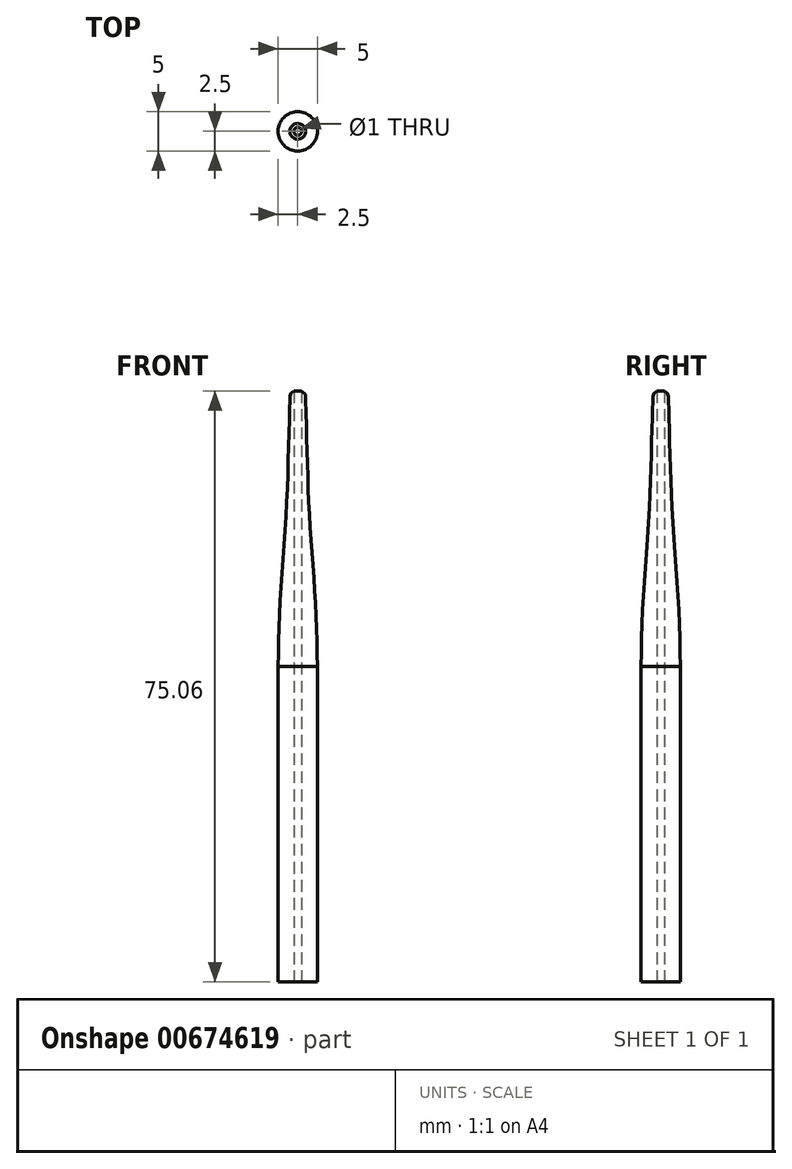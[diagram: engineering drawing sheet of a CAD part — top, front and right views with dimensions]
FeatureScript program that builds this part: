
annotation { "Feature Type Name" : "Feature", "Feature Type Description" : "" }
export const myFeature = defineFeature(function(context is Context, id is Id, definition is map)
    precondition{}
    {
        {
            var Q0;
            Q0=qCreatedBy(makeId("Right.planeOp"),FACE);
            var sketch = newSketch(context, id + "F0", { "sketchPlane" : qUnion([Q0])});
            skLineSegment(sketch, "E0.right", {"start": v(-2.5, 12.56) * mm, "end": v(-2.5, 0) * mm});
            skPoint(sketch, "E0.middle", {"position": v(0, 0) * mm});
            skLineSegment(sketch, "E1.right", {"start": v(-0.5, 0) * mm, "end": v(-0.5, 47.56) * mm});
            skFitSpline(sketch, "E2", {"points": [v(-2.5, 12.56) * mm, v(-2.22, 21.1) * mm, v(-1.53, 30.92) * mm, v(-1.16, 40.59) * mm, v(-1, 46.59) * mm, v(-0.92, 47.22) * mm, v(-0.5, 47.56) * mm], "startDerivative": vector(0.72, 37.68) * mm, "endDerivative": vector(9.02, 5.7) * mm});
            skLineSegment(sketch, "E3", {"start": v(0, -0.42) * mm, "end": v(0, 3.42) * mm});
            skLineSegment(sketch, "E4.top", {"start": v(-0.5, -27.5) * mm, "end": v(-2.5, -27.5) * mm});
            skLineSegment(sketch, "E4.left", {"start": v(-0.5, 0) * mm, "end": v(-0.5, -27.5) * mm});
            skLineSegment(sketch, "E4.right", {"start": v(-2.5, 0) * mm, "end": v(-2.5, -27.5) * mm});
            skSolve(sketch);
        }
        {
            var Q0;
            Q0 = qSketchRegion(id + "F0", true);
            var Q1;
            Q1=sQuery(id+"F0.wireOp",EDGE,"E3");
            revolve(context, id + "F1", {"entities" : qUnion([Q0]), "axis" : qUnion([Q1]), "revolveType" : RevolveType.FULL});
        }
    });
